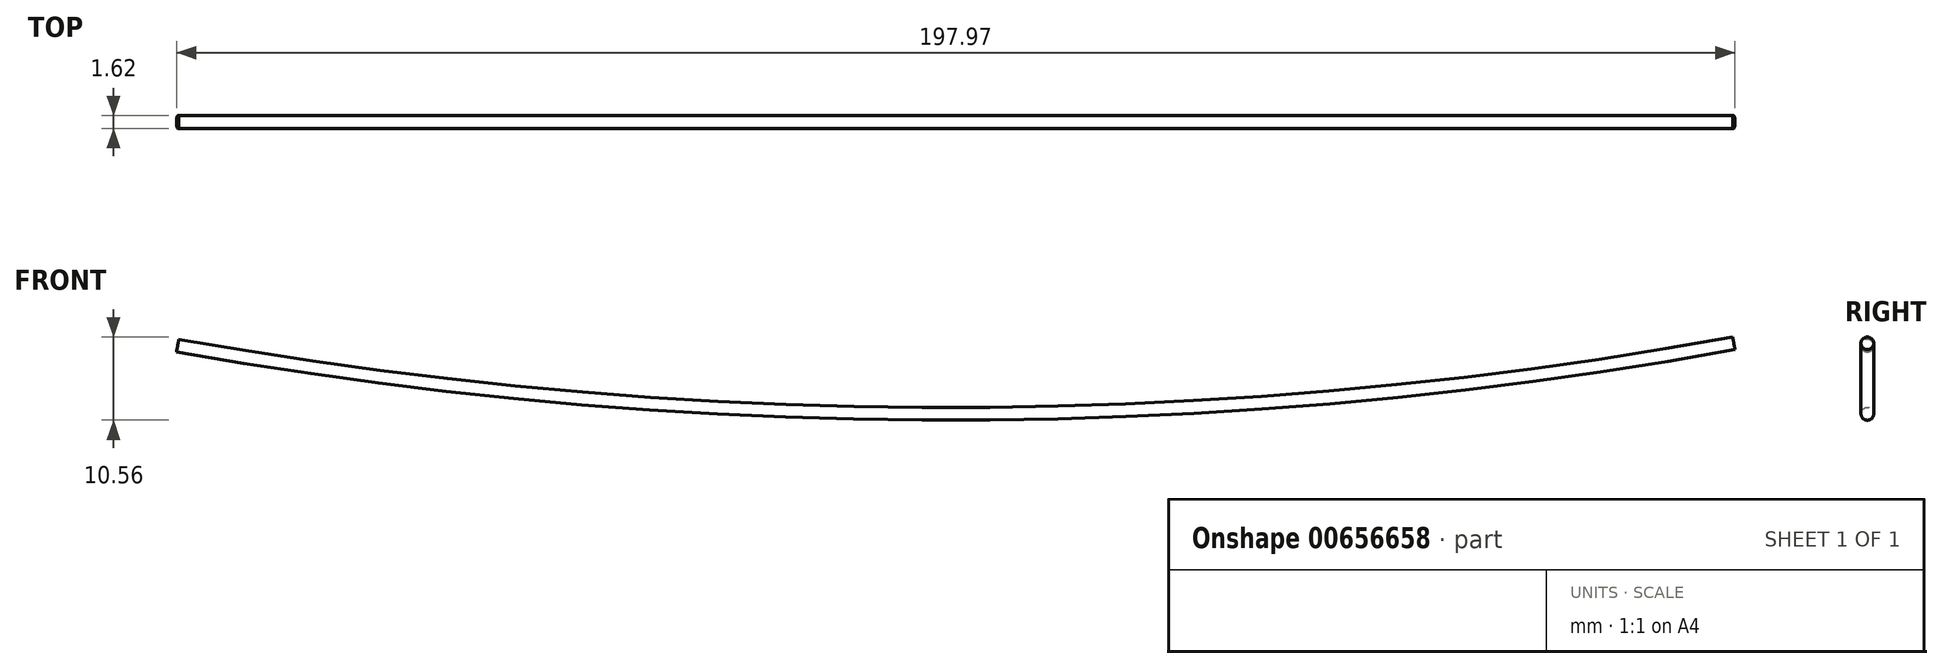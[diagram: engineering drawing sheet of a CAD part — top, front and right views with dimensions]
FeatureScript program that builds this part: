
annotation { "Feature Type Name" : "Feature", "Feature Type Description" : "" }
export const myFeature = defineFeature(function(context is Context, id is Id, definition is map)
    precondition{}
    {
        {
            var Q0;
            Q0=qCreatedBy(makeId("Front.planeOp"),FACE);
            var sketch = newSketch(context, id + "F0", { "sketchPlane" : qUnion([Q0])});
            skArc(sketch, "E0", {"start": v(-99.16, 55.75) * mm, "mid": v(-0.27, 47.07) * mm, "end": v(98.6, 56.04) * mm});
            skSolve(sketch);
        }
        {
            var Q0;
            Q0=qCreatedBy(makeId("Right.planeOp"),FACE);
            var sketch = newSketch(context, id + "F1", { "sketchPlane" : qUnion([Q0])});
            skCircle(sketch, "E1", {"center": v(0, 47.29) * mm, "radius": 0.8 * mm});
            skSolve(sketch);
        }
        {
            var Q0;
            Q0=makeQuery(id+"F1.imprint","IMPRINT",FACE,{"disambiguationData":[TD([[makeQuery(id+"F1.imprint","IMPRINT",EDGE,{"derivedFrom":sQuery(id+"F1.wireOp",EDGE,"E1")}),1.0]])]});
            var Q1;
            Q1=sQuery(id+"F0.wireOp",EDGE,"E0");
            sweep(context, id + "F2", {"profiles" : qUnion([Q0]), "path" : qUnion([Q1])});
        }
    });
